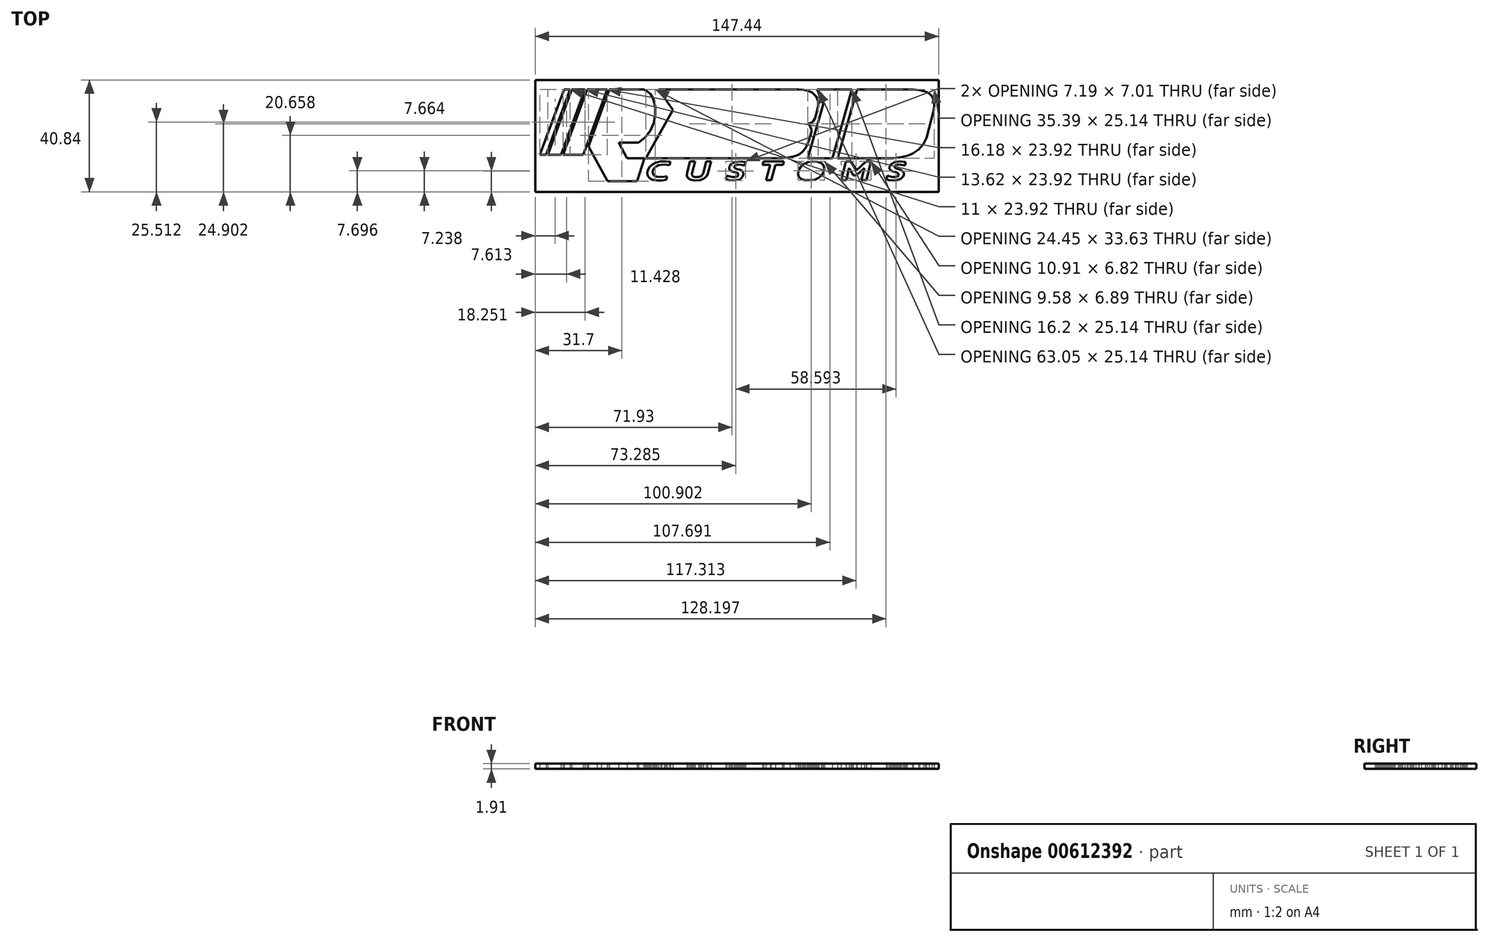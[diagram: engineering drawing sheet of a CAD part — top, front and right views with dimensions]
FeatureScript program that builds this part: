
annotation { "Feature Type Name" : "Feature", "Feature Type Description" : "" }
export const myFeature = defineFeature(function(context is Context, id is Id, definition is map)
    precondition{}
    {
        {
            var Q0;
            Q0=qCreatedBy(makeId("Top.planeOp"),FACE);
            var sketch = newSketch(context, id + "F0", { "sketchPlane" : qUnion([Q0])});
            skLineSegment(sketch, "E0", {"start": v(40.42, -9.55) * mm, "end": v(42.26, -9.55) * mm});
            skLineSegment(sketch, "E1", {"start": v(46.05, -16.37) * mm, "end": v(47.89, -16.37) * mm});
            skLineSegment(sketch, "E2", {"start": v(47.82, -9.55) * mm, "end": v(49.6, -9.55) * mm});
            skLineSegment(sketch, "E3", {"start": v(47.16, -11.96) * mm, "end": v(46.05, -16.37) * mm});
            skLineSegment(sketch, "E4", {"start": v(44.27, -14.59) * mm, "end": v(47.16, -11.96) * mm});
            skLineSegment(sketch, "E5", {"start": v(43.16, -14.59) * mm, "end": v(44.27, -14.59) * mm});
            skLineSegment(sketch, "E6", {"start": v(41.6, -11.98) * mm, "end": v(43.16, -14.59) * mm});
            skLineSegment(sketch, "E7", {"start": v(49.6, -9.55) * mm, "end": v(47.89, -16.37) * mm});
            skLineSegment(sketch, "E8", {"start": v(44.21, -12.83) * mm, "end": v(47.82, -9.55) * mm});
            skLineSegment(sketch, "E9", {"start": v(42.26, -9.55) * mm, "end": v(44.21, -12.83) * mm});
            skLineSegment(sketch, "E10", {"start": v(41.6, -11.98) * mm, "end": v(40.5, -16.37) * mm});
            skLineSegment(sketch, "E11", {"start": v(40.42, -9.55) * mm, "end": v(38.7, -16.37) * mm});
            skLineSegment(sketch, "E12", {"start": v(28.33, -9.55) * mm, "end": v(26.64, -9.76) * mm});
            skLineSegment(sketch, "E13", {"start": v(26.64, -9.76) * mm, "end": v(24.97, -10.5) * mm});
            skLineSegment(sketch, "E14", {"start": v(24.97, -10.5) * mm, "end": v(23.75, -11.65) * mm});
            skLineSegment(sketch, "E15", {"start": v(23.75, -11.65) * mm, "end": v(23.18, -12.71) * mm});
            skLineSegment(sketch, "E16", {"start": v(23.18, -12.71) * mm, "end": v(22.95, -13.91) * mm});
            skLineSegment(sketch, "E17", {"start": v(22.95, -13.91) * mm, "end": v(23.15, -15.07) * mm});
            skLineSegment(sketch, "E18", {"start": v(23.15, -15.07) * mm, "end": v(23.88, -15.86) * mm});
            skLineSegment(sketch, "E19", {"start": v(23.88, -15.86) * mm, "end": v(25.38, -16.36) * mm});
            skLineSegment(sketch, "E20", {"start": v(25.38, -16.36) * mm, "end": v(27.12, -16.44) * mm});
            skLineSegment(sketch, "E21", {"start": v(27.12, -16.44) * mm, "end": v(28.98, -16.25) * mm});
            skLineSegment(sketch, "E22", {"start": v(28.98, -16.25) * mm, "end": v(30.55, -15.5) * mm});
            skLineSegment(sketch, "E23", {"start": v(30.55, -15.5) * mm, "end": v(31.72, -14.43) * mm});
            skLineSegment(sketch, "E24", {"start": v(31.72, -14.43) * mm, "end": v(32.25, -13.43) * mm});
            skLineSegment(sketch, "E25", {"start": v(32.25, -13.43) * mm, "end": v(32.53, -12.09) * mm});
            skLineSegment(sketch, "E26", {"start": v(32.53, -12.09) * mm, "end": v(32.23, -10.87) * mm});
            skLineSegment(sketch, "E27", {"start": v(32.23, -10.87) * mm, "end": v(31.4, -10.13) * mm});
            skLineSegment(sketch, "E28", {"start": v(31.4, -10.13) * mm, "end": v(29.92, -9.63) * mm});
            skLineSegment(sketch, "E29", {"start": v(29.92, -9.63) * mm, "end": v(28.33, -9.55) * mm});
            skLineSegment(sketch, "E30", {"start": v(17.42, -10.84) * mm, "end": v(17.74, -9.55) * mm});
            skLineSegment(sketch, "E31", {"start": v(14.63, -10.84) * mm, "end": v(17.42, -10.84) * mm});
            skLineSegment(sketch, "E32", {"start": v(13.16, -16.37) * mm, "end": v(14.63, -10.84) * mm});
            skLineSegment(sketch, "E33", {"start": v(11.28, -16.37) * mm, "end": v(11.47, -16.37) * mm});
            skLineSegment(sketch, "E34", {"start": v(12.75, -10.84) * mm, "end": v(11.28, -16.37) * mm});
            skLineSegment(sketch, "E35", {"start": v(9.96, -10.84) * mm, "end": v(12.75, -10.84) * mm});
            skLineSegment(sketch, "E36", {"start": v(10.28, -9.55) * mm, "end": v(9.96, -10.84) * mm});
            skLineSegment(sketch, "E37", {"start": v(55.5, -14.69) * mm, "end": v(55.12, -16.02) * mm});
            skLineSegment(sketch, "E38", {"start": v(62.31, -9.82) * mm, "end": v(60.42, -9.53) * mm});
            skLineSegment(sketch, "E39", {"start": v(60.42, -9.53) * mm, "end": v(58.37, -9.72) * mm});
            skLineSegment(sketch, "E40", {"start": v(58.37, -9.72) * mm, "end": v(56.95, -10.49) * mm});
            skLineSegment(sketch, "E41", {"start": v(56.95, -10.49) * mm, "end": v(56.44, -11.2) * mm});
            skLineSegment(sketch, "E42", {"start": v(56.44, -11.2) * mm, "end": v(56.3, -12.06) * mm});
            skLineSegment(sketch, "E43", {"start": v(56.3, -12.06) * mm, "end": v(56.52, -12.6) * mm});
            skLineSegment(sketch, "E44", {"start": v(56.52, -12.6) * mm, "end": v(57.02, -12.95) * mm});
            skLineSegment(sketch, "E45", {"start": v(57.02, -12.95) * mm, "end": v(57.56, -13.17) * mm});
            skLineSegment(sketch, "E46", {"start": v(57.56, -13.17) * mm, "end": v(58.24, -13.4) * mm});
            skLineSegment(sketch, "E47", {"start": v(58.24, -13.4) * mm, "end": v(58.94, -13.62) * mm});
            skLineSegment(sketch, "E48", {"start": v(58.94, -13.62) * mm, "end": v(59.4, -13.82) * mm});
            skLineSegment(sketch, "E49", {"start": v(59.4, -13.82) * mm, "end": v(59.67, -14.18) * mm});
            skLineSegment(sketch, "E50", {"start": v(59.67, -14.18) * mm, "end": v(59.68, -14.56) * mm});
            skLineSegment(sketch, "E51", {"start": v(59.68, -14.56) * mm, "end": v(59.34, -14.98) * mm});
            skLineSegment(sketch, "E52", {"start": v(59.34, -14.98) * mm, "end": v(58.5, -15.25) * mm});
            skLineSegment(sketch, "E53", {"start": v(58.5, -15.25) * mm, "end": v(57.48, -15.22) * mm});
            skLineSegment(sketch, "E54", {"start": v(57.48, -15.22) * mm, "end": v(56.34, -15.01) * mm});
            skLineSegment(sketch, "E55", {"start": v(56.34, -15.01) * mm, "end": v(55.5, -14.69) * mm});
            skLineSegment(sketch, "E56", {"start": v(62.05, -11.04) * mm, "end": v(60.8, -10.76) * mm});
            skLineSegment(sketch, "E57", {"start": v(60.8, -10.76) * mm, "end": v(59.61, -10.67) * mm});
            skLineSegment(sketch, "E58", {"start": v(59.61, -10.67) * mm, "end": v(58.6, -10.88) * mm});
            skLineSegment(sketch, "E59", {"start": v(58.6, -10.88) * mm, "end": v(58.19, -11.37) * mm});
            skLineSegment(sketch, "E60", {"start": v(58.19, -11.37) * mm, "end": v(58.28, -11.84) * mm});
            skLineSegment(sketch, "E61", {"start": v(58.28, -11.84) * mm, "end": v(58.79, -12.13) * mm});
            skLineSegment(sketch, "E62", {"start": v(58.79, -12.13) * mm, "end": v(59.58, -12.38) * mm});
            skLineSegment(sketch, "E63", {"start": v(59.58, -12.38) * mm, "end": v(60.29, -12.61) * mm});
            skLineSegment(sketch, "E64", {"start": v(60.29, -12.61) * mm, "end": v(60.77, -12.83) * mm});
            skLineSegment(sketch, "E65", {"start": v(60.77, -12.83) * mm, "end": v(61.5, -13.41) * mm});
            skLineSegment(sketch, "E66", {"start": v(61.5, -13.41) * mm, "end": v(61.6, -14.2) * mm});
            skLineSegment(sketch, "E67", {"start": v(61.6, -14.2) * mm, "end": v(61.33, -15.03) * mm});
            skLineSegment(sketch, "E68", {"start": v(61.33, -15.03) * mm, "end": v(60.68, -15.74) * mm});
            skLineSegment(sketch, "E69", {"start": v(60.68, -15.74) * mm, "end": v(59.85, -16.19) * mm});
            skLineSegment(sketch, "E70", {"start": v(59.85, -16.19) * mm, "end": v(58.8, -16.44) * mm});
            skLineSegment(sketch, "E71", {"start": v(58.8, -16.44) * mm, "end": v(57.5, -16.54) * mm});
            skLineSegment(sketch, "E72", {"start": v(57.5, -16.54) * mm, "end": v(56.2, -16.35) * mm});
            skLineSegment(sketch, "E73", {"start": v(56.2, -16.35) * mm, "end": v(55.12, -16.02) * mm});
            skLineSegment(sketch, "E74", {"start": v(62.31, -9.82) * mm, "end": v(62.05, -11.04) * mm});
            skLineSegment(sketch, "E75", {"start": v(-3.1, -14.7) * mm, "end": v(-3.47, -16.03) * mm});
            skLineSegment(sketch, "E76", {"start": v(3.72, -9.83) * mm, "end": v(1.82, -9.54) * mm});
            skLineSegment(sketch, "E77", {"start": v(1.82, -9.54) * mm, "end": v(-0.22, -9.73) * mm});
            skLineSegment(sketch, "E78", {"start": v(-0.22, -9.73) * mm, "end": v(-1.65, -10.5) * mm});
            skLineSegment(sketch, "E79", {"start": v(-1.65, -10.5) * mm, "end": v(-2.15, -11.2) * mm});
            skLineSegment(sketch, "E80", {"start": v(-2.15, -11.2) * mm, "end": v(-2.3, -12.06) * mm});
            skLineSegment(sketch, "E81", {"start": v(-2.3, -12.06) * mm, "end": v(-2.07, -12.61) * mm});
            skLineSegment(sketch, "E82", {"start": v(-2.07, -12.61) * mm, "end": v(-1.57, -12.96) * mm});
            skLineSegment(sketch, "E83", {"start": v(-1.57, -12.96) * mm, "end": v(-1.04, -13.18) * mm});
            skLineSegment(sketch, "E84", {"start": v(-1.04, -13.18) * mm, "end": v(-0.35, -13.4) * mm});
            skLineSegment(sketch, "E85", {"start": v(-0.35, -13.4) * mm, "end": v(0.34, -13.63) * mm});
            skLineSegment(sketch, "E86", {"start": v(0.34, -13.63) * mm, "end": v(0.8, -13.83) * mm});
            skLineSegment(sketch, "E87", {"start": v(0.8, -13.83) * mm, "end": v(1.08, -14.19) * mm});
            skLineSegment(sketch, "E88", {"start": v(1.08, -14.19) * mm, "end": v(1.08, -14.57) * mm});
            skLineSegment(sketch, "E89", {"start": v(1.08, -14.57) * mm, "end": v(0.75, -15) * mm});
            skLineSegment(sketch, "E90", {"start": v(0.75, -15) * mm, "end": v(-0.1, -15.26) * mm});
            skLineSegment(sketch, "E91", {"start": v(-0.1, -15.26) * mm, "end": v(-1.11, -15.23) * mm});
            skLineSegment(sketch, "E92", {"start": v(-1.11, -15.23) * mm, "end": v(-2.25, -15.02) * mm});
            skLineSegment(sketch, "E93", {"start": v(-2.25, -15.02) * mm, "end": v(-3.1, -14.7) * mm});
            skLineSegment(sketch, "E94", {"start": v(3.46, -11.04) * mm, "end": v(2.2, -10.77) * mm});
            skLineSegment(sketch, "E95", {"start": v(2.2, -10.77) * mm, "end": v(1.02, -10.68) * mm});
            skLineSegment(sketch, "E96", {"start": v(1.02, -10.68) * mm, "end": v(0.02, -10.89) * mm});
            skLineSegment(sketch, "E97", {"start": v(0.02, -10.89) * mm, "end": v(-0.4, -11.38) * mm});
            skLineSegment(sketch, "E98", {"start": v(-0.4, -11.38) * mm, "end": v(-0.31, -11.85) * mm});
            skLineSegment(sketch, "E99", {"start": v(-0.31, -11.85) * mm, "end": v(0.2, -12.14) * mm});
            skLineSegment(sketch, "E100", {"start": v(0.2, -12.14) * mm, "end": v(0.99, -12.4) * mm});
            skLineSegment(sketch, "E101", {"start": v(0.99, -12.4) * mm, "end": v(1.7, -12.62) * mm});
            skLineSegment(sketch, "E102", {"start": v(1.7, -12.62) * mm, "end": v(2.18, -12.84) * mm});
            skLineSegment(sketch, "E103", {"start": v(2.18, -12.84) * mm, "end": v(2.9, -13.42) * mm});
            skLineSegment(sketch, "E104", {"start": v(2.9, -13.42) * mm, "end": v(3, -14.21) * mm});
            skLineSegment(sketch, "E105", {"start": v(3, -14.21) * mm, "end": v(2.73, -15.04) * mm});
            skLineSegment(sketch, "E106", {"start": v(2.73, -15.04) * mm, "end": v(2.08, -15.75) * mm});
            skLineSegment(sketch, "E107", {"start": v(2.08, -15.75) * mm, "end": v(1.25, -16.2) * mm});
            skLineSegment(sketch, "E108", {"start": v(1.25, -16.2) * mm, "end": v(0.2, -16.45) * mm});
            skLineSegment(sketch, "E109", {"start": v(0.2, -16.45) * mm, "end": v(-1.08, -16.55) * mm});
            skLineSegment(sketch, "E110", {"start": v(-1.08, -16.55) * mm, "end": v(-2.4, -16.36) * mm});
            skLineSegment(sketch, "E111", {"start": v(-2.4, -16.36) * mm, "end": v(-3.47, -16.03) * mm});
            skLineSegment(sketch, "E112", {"start": v(3.72, -9.83) * mm, "end": v(3.46, -11.04) * mm});
            skLineSegment(sketch, "E113", {"start": v(-10.66, -9.55) * mm, "end": v(-8.86, -9.55) * mm});
            skLineSegment(sketch, "E114", {"start": v(-15.84, -13.84) * mm, "end": v(-15.9, -14.3) * mm});
            skLineSegment(sketch, "E115", {"start": v(-15.9, -14.3) * mm, "end": v(-15.74, -14.76) * mm});
            skLineSegment(sketch, "E116", {"start": v(-15.74, -14.76) * mm, "end": v(-15.37, -15.07) * mm});
            skLineSegment(sketch, "E117", {"start": v(-15.37, -15.07) * mm, "end": v(-14.82, -15.24) * mm});
            skLineSegment(sketch, "E118", {"start": v(-14.82, -15.24) * mm, "end": v(-13.42, -15.23) * mm});
            skLineSegment(sketch, "E119", {"start": v(-13.42, -15.23) * mm, "end": v(-12.35, -14.87) * mm});
            skLineSegment(sketch, "E120", {"start": v(-12.35, -14.87) * mm, "end": v(-11.82, -14.03) * mm});
            skLineSegment(sketch, "E121", {"start": v(-17.67, -13.74) * mm, "end": v(-17.74, -14.84) * mm});
            skLineSegment(sketch, "E122", {"start": v(-17.74, -14.84) * mm, "end": v(-17.26, -15.76) * mm});
            skLineSegment(sketch, "E123", {"start": v(-17.26, -15.76) * mm, "end": v(-16.24, -16.3) * mm});
            skLineSegment(sketch, "E124", {"start": v(-16.24, -16.3) * mm, "end": v(-14.86, -16.5) * mm});
            skLineSegment(sketch, "E125", {"start": v(-14.86, -16.5) * mm, "end": v(-12.9, -16.4) * mm});
            skLineSegment(sketch, "E126", {"start": v(-12.9, -16.4) * mm, "end": v(-11.66, -15.9) * mm});
            skLineSegment(sketch, "E127", {"start": v(-11.66, -15.9) * mm, "end": v(-10.58, -15.08) * mm});
            skLineSegment(sketch, "E128", {"start": v(-10.58, -15.08) * mm, "end": v(-10.05, -14.17) * mm});
            skLineSegment(sketch, "E129", {"start": v(-8.86, -9.55) * mm, "end": v(-10.05, -14.17) * mm});
            skLineSegment(sketch, "E130", {"start": v(-10.66, -9.55) * mm, "end": v(-11.82, -14.03) * mm});
            skLineSegment(sketch, "E131", {"start": v(-14.73, -9.55) * mm, "end": v(-15.84, -13.84) * mm});
            skLineSegment(sketch, "E132", {"start": v(-16.58, -9.55) * mm, "end": v(-17.67, -13.74) * mm});
            skLineSegment(sketch, "E133", {"start": v(11.47, -16.37) * mm, "end": v(13.16, -16.37) * mm});
            skLineSegment(sketch, "E134", {"start": v(-16.58, -9.55) * mm, "end": v(-14.73, -9.55) * mm});
            skLineSegment(sketch, "E135", {"start": v(-24.91, -15.04) * mm, "end": v(-25.17, -16.21) * mm});
            skLineSegment(sketch, "E136", {"start": v(-23.75, -9.7) * mm, "end": v(-25.46, -9.49) * mm});
            skLineSegment(sketch, "E137", {"start": v(-25.46, -9.49) * mm, "end": v(-27.31, -9.52) * mm});
            skLineSegment(sketch, "E138", {"start": v(-27.31, -9.52) * mm, "end": v(-29.2, -10.02) * mm});
            skLineSegment(sketch, "E139", {"start": v(-29.2, -10.02) * mm, "end": v(-30.33, -10.61) * mm});
            skLineSegment(sketch, "E140", {"start": v(-30.33, -10.61) * mm, "end": v(-31.37, -11.6) * mm});
            skLineSegment(sketch, "E141", {"start": v(-31.37, -11.6) * mm, "end": v(-31.97, -12.67) * mm});
            skLineSegment(sketch, "E142", {"start": v(-31.97, -12.67) * mm, "end": v(-32.2, -13.7) * mm});
            skLineSegment(sketch, "E143", {"start": v(-32.2, -13.7) * mm, "end": v(-32.1, -14.5) * mm});
            skLineSegment(sketch, "E144", {"start": v(-32.1, -14.5) * mm, "end": v(-31.75, -15.24) * mm});
            skLineSegment(sketch, "E145", {"start": v(-31.75, -15.24) * mm, "end": v(-31.15, -15.81) * mm});
            skLineSegment(sketch, "E146", {"start": v(-31.15, -15.81) * mm, "end": v(-30.33, -16.2) * mm});
            skLineSegment(sketch, "E147", {"start": v(-30.33, -16.2) * mm, "end": v(-28.66, -16.51) * mm});
            skLineSegment(sketch, "E148", {"start": v(-28.66, -16.51) * mm, "end": v(-26.83, -16.51) * mm});
            skLineSegment(sketch, "E149", {"start": v(-26.83, -16.51) * mm, "end": v(-25.17, -16.21) * mm});
            skLineSegment(sketch, "E150", {"start": v(-24.03, -10.99) * mm, "end": v(-26.03, -10.68) * mm});
            skLineSegment(sketch, "E151", {"start": v(-26.03, -10.68) * mm, "end": v(-28.04, -10.96) * mm});
            skLineSegment(sketch, "E152", {"start": v(-28.04, -10.96) * mm, "end": v(-29.02, -11.46) * mm});
            skLineSegment(sketch, "E153", {"start": v(-29.02, -11.46) * mm, "end": v(-29.77, -12.2) * mm});
            skLineSegment(sketch, "E154", {"start": v(-29.77, -12.2) * mm, "end": v(-30.16, -12.97) * mm});
            skLineSegment(sketch, "E155", {"start": v(-30.16, -12.97) * mm, "end": v(-30.23, -13.75) * mm});
            skLineSegment(sketch, "E156", {"start": v(-30.23, -13.75) * mm, "end": v(-29.78, -14.65) * mm});
            skLineSegment(sketch, "E157", {"start": v(-29.78, -14.65) * mm, "end": v(-28.8, -15.1) * mm});
            skLineSegment(sketch, "E158", {"start": v(-28.8, -15.1) * mm, "end": v(-26.94, -15.3) * mm});
            skLineSegment(sketch, "E159", {"start": v(-26.94, -15.3) * mm, "end": v(-24.91, -15.04) * mm});
            skLineSegment(sketch, "E160", {"start": v(-23.75, -9.7) * mm, "end": v(-24.03, -10.99) * mm});
            skLineSegment(sketch, "E161", {"start": v(69.84, -0.9) * mm, "end": v(68.76, -3.12) * mm});
            skLineSegment(sketch, "E162", {"start": v(68.76, -3.12) * mm, "end": v(67, -5.17) * mm});
            skLineSegment(sketch, "E163", {"start": v(67, -5.17) * mm, "end": v(64.73, -6.7) * mm});
            skLineSegment(sketch, "E164", {"start": v(64.73, -6.7) * mm, "end": v(62.78, -7.48) * mm});
            skLineSegment(sketch, "E165", {"start": v(62.78, -7.48) * mm, "end": v(60.46, -8.02) * mm});
            skLineSegment(sketch, "E166", {"start": v(60.46, -8.02) * mm, "end": v(57.74, -8.33) * mm});
            skLineSegment(sketch, "E167", {"start": v(42.63, 16.81) * mm, "end": v(29.83, 16.81) * mm});
            skLineSegment(sketch, "E168", {"start": v(37.34, -8.33) * mm, "end": v(57.74, -8.33) * mm});
            skLineSegment(sketch, "E169", {"start": v(26.43, -8.33) * mm, "end": v(35.44, -8.33) * mm});
            skLineSegment(sketch, "E170", {"start": v(23.18, 16.81) * mm, "end": v(-0.77, 16.81) * mm});
            skLineSegment(sketch, "E171", {"start": v(-8.5, 16.81) * mm, "end": v(-28.07, 16.81) * mm});
            skLineSegment(sketch, "E172", {"start": v(2.73, -8.33) * mm, "end": v(17.25, -8.33) * mm});
            skLineSegment(sketch, "E173", {"start": v(-22.78, 9.31) * mm, "end": v(-32.76, -8.33) * mm});
            skLineSegment(sketch, "E174", {"start": v(29.83, 16.81) * mm, "end": v(32.18, 11.5) * mm});
            skLineSegment(sketch, "E175", {"start": v(32.18, 11.5) * mm, "end": v(26.43, -8.33) * mm});
            skLineSegment(sketch, "E176", {"start": v(42.63, 16.81) * mm, "end": v(35.44, -8.33) * mm});
            skLineSegment(sketch, "E177", {"start": v(44.53, 16.81) * mm, "end": v(37.34, -8.33) * mm});
            skLineSegment(sketch, "E178", {"start": v(72.6, 9.4) * mm, "end": v(72.73, 11.14) * mm});
            skLineSegment(sketch, "E179", {"start": v(72.73, 11.14) * mm, "end": v(72.5, 12.82) * mm});
            skLineSegment(sketch, "E180", {"start": v(72.5, 12.82) * mm, "end": v(71.77, 14.33) * mm});
            skLineSegment(sketch, "E181", {"start": v(71.77, 14.33) * mm, "end": v(70.74, 15.37) * mm});
            skLineSegment(sketch, "E182", {"start": v(70.74, 15.37) * mm, "end": v(69.33, 16.02) * mm});
            skLineSegment(sketch, "E183", {"start": v(69.33, 16.02) * mm, "end": v(67.4, 16.56) * mm});
            skLineSegment(sketch, "E184", {"start": v(67.4, 16.56) * mm, "end": v(65.13, 16.81) * mm});
            skLineSegment(sketch, "E185", {"start": v(72.6, 9.4) * mm, "end": v(69.84, -0.9) * mm});
            skLineSegment(sketch, "E186", {"start": v(26.33, 4.26) * mm, "end": v(27.18, 4.4) * mm});
            skLineSegment(sketch, "E187", {"start": v(27.18, 4.4) * mm, "end": v(27.93, 4.66) * mm});
            skLineSegment(sketch, "E188", {"start": v(27.93, 4.66) * mm, "end": v(28.5, 5.19) * mm});
            skLineSegment(sketch, "E189", {"start": v(28.5, 5.19) * mm, "end": v(29.07, 6.28) * mm});
            skLineSegment(sketch, "E190", {"start": v(29.07, 6.28) * mm, "end": v(29.82, 8.46) * mm});
            skLineSegment(sketch, "E191", {"start": v(29.82, 8.46) * mm, "end": v(30.3, 10.75) * mm});
            skLineSegment(sketch, "E192", {"start": v(30.3, 10.75) * mm, "end": v(30.27, 12.45) * mm});
            skLineSegment(sketch, "E193", {"start": v(30.27, 12.45) * mm, "end": v(29.52, 14.24) * mm});
            skLineSegment(sketch, "E194", {"start": v(29.52, 14.24) * mm, "end": v(28.06, 15.6) * mm});
            skLineSegment(sketch, "E195", {"start": v(28.06, 15.6) * mm, "end": v(26.62, 16.23) * mm});
            skLineSegment(sketch, "E196", {"start": v(26.62, 16.23) * mm, "end": v(24.88, 16.66) * mm});
            skLineSegment(sketch, "E197", {"start": v(24.88, 16.66) * mm, "end": v(23.18, 16.81) * mm});
            skLineSegment(sketch, "E198", {"start": v(26.33, 4.26) * mm, "end": v(26.98, 3.8) * mm});
            skLineSegment(sketch, "E199", {"start": v(26.98, 3.8) * mm, "end": v(27.5, 3.08) * mm});
            skLineSegment(sketch, "E200", {"start": v(27.5, 3.08) * mm, "end": v(27.8, 2.23) * mm});
            skLineSegment(sketch, "E201", {"start": v(27.8, 2.23) * mm, "end": v(27.8, 1.48) * mm});
            skLineSegment(sketch, "E202", {"start": v(27.8, 1.48) * mm, "end": v(27.47, 0.1) * mm});
            skLineSegment(sketch, "E203", {"start": v(27.47, 0.1) * mm, "end": v(26.82, -1.9) * mm});
            skLineSegment(sketch, "E204", {"start": v(26.82, -1.9) * mm, "end": v(26.2, -3.5) * mm});
            skLineSegment(sketch, "E205", {"start": v(26.2, -3.5) * mm, "end": v(25.56, -4.77) * mm});
            skLineSegment(sketch, "E206", {"start": v(25.56, -4.77) * mm, "end": v(24.6, -5.92) * mm});
            skLineSegment(sketch, "E207", {"start": v(24.6, -5.92) * mm, "end": v(23.49, -6.81) * mm});
            skLineSegment(sketch, "E208", {"start": v(23.49, -6.81) * mm, "end": v(22.2, -7.5) * mm});
            skLineSegment(sketch, "E209", {"start": v(22.2, -7.5) * mm, "end": v(19.95, -8) * mm});
            skLineSegment(sketch, "E210", {"start": v(19.95, -8) * mm, "end": v(17.25, -8.33) * mm});
            skLineSegment(sketch, "E211", {"start": v(-33.51, 16.81) * mm, "end": v(-32.12, 16.04) * mm});
            skLineSegment(sketch, "E212", {"start": v(-32.12, 16.04) * mm, "end": v(-30.97, 14.97) * mm});
            skLineSegment(sketch, "E213", {"start": v(-30.97, 14.97) * mm, "end": v(-30.1, 13.47) * mm});
            skLineSegment(sketch, "E214", {"start": v(-30.1, 13.47) * mm, "end": v(-29.23, 10.61) * mm});
            skLineSegment(sketch, "E215", {"start": v(-29.23, 10.61) * mm, "end": v(-29.24, 7.62) * mm});
            skLineSegment(sketch, "E216", {"start": v(-29.24, 7.62) * mm, "end": v(-29.86, 4.52) * mm});
            skLineSegment(sketch, "E217", {"start": v(-29.86, 4.52) * mm, "end": v(-31.1, 1.59) * mm});
            skLineSegment(sketch, "E218", {"start": v(-31.1, 1.59) * mm, "end": v(-33.02, -0.8) * mm});
            skLineSegment(sketch, "E219", {"start": v(-33.02, -0.8) * mm, "end": v(-35.37, -2.66) * mm});
            skLineSegment(sketch, "E220", {"start": v(-33.51, 16.81) * mm, "end": v(-46.1, 16.81) * mm});
            skLineSegment(sketch, "E221", {"start": v(-5.07, -8.33) * mm, "end": v(2.3, -8.33) * mm});
            skLineSegment(sketch, "E222", {"start": v(38.7, -16.37) * mm, "end": v(40.5, -16.37) * mm});
            skLineSegment(sketch, "E223", {"start": v(28.33, -9.55) * mm, "end": v(29.1, -9.55) * mm});
            skLineSegment(sketch, "E224", {"start": v(10.28, -9.55) * mm, "end": v(17.74, -9.55) * mm});
            skLineSegment(sketch, "E225", {"start": v(1.03, -9.55) * mm, "end": v(2.06, -9.55) * mm});
            skLineSegment(sketch, "E226", {"start": v(65.13, 16.81) * mm, "end": v(44.53, 16.81) * mm});
            skLineSegment(sketch, "E227", {"start": v(-49, 8.95) * mm, "end": v(-46.1, 16.81) * mm});
            skLineSegment(sketch, "E228", {"start": v(-50.53, 4.54) * mm, "end": v(-53.69, -4.04) * mm});
            skLineSegment(sketch, "E229", {"start": v(-53.69, -4.04) * mm, "end": v(-46.73, -16.81) * mm});
            skLineSegment(sketch, "E230", {"start": v(-46.73, -16.81) * mm, "end": v(-35.85, -16.81) * mm});
            skLineSegment(sketch, "E231", {"start": v(-35.85, -16.81) * mm, "end": v(-33.28, -8.33) * mm});
            skLineSegment(sketch, "E232", {"start": v(-33.28, -8.33) * mm, "end": v(-39.56, -8.33) * mm});
            skLineSegment(sketch, "E233", {"start": v(-39.56, -8.33) * mm, "end": v(-42.64, -2.66) * mm});
            skLineSegment(sketch, "E234", {"start": v(-42.64, -2.66) * mm, "end": v(-35.37, -2.66) * mm});
            skLineSegment(sketch, "E235", {"start": v(-32.76, -8.33) * mm, "end": v(-22.07, -8.33) * mm});
            skLineSegment(sketch, "E236", {"start": v(-28.07, 16.81) * mm, "end": v(-22.78, 9.31) * mm});
            skLineSegment(sketch, "E237", {"start": v(-22.07, -8.33) * mm, "end": v(-5.07, -8.33) * mm});
            skLineSegment(sketch, "E238", {"start": v(-49, 8.95) * mm, "end": v(-50.53, 4.54) * mm});
            skLineSegment(sketch, "E239", {"start": v(-8.5, 16.81) * mm, "end": v(-0.77, 16.81) * mm});
            skLineSegment(sketch, "E240", {"start": v(2.3, -8.33) * mm, "end": v(2.73, -8.33) * mm});
            skLineSegment(sketch, "E241", {"start": v(-71.42, -7.1) * mm, "end": v(-62.62, 16.81) * mm});
            skLineSegment(sketch, "E242", {"start": v(-55.62, -7.1) * mm, "end": v(-63, -7.1) * mm});
            skLineSegment(sketch, "E243", {"start": v(-60.42, 16.81) * mm, "end": v(-69.22, -7.1) * mm});
            skLineSegment(sketch, "E244", {"start": v(-68.54, -7.1) * mm, "end": v(-59.74, 16.81) * mm});
            skLineSegment(sketch, "E245", {"start": v(-54.92, 16.81) * mm, "end": v(-63.73, -7.1) * mm});
            skLineSegment(sketch, "E246", {"start": v(-63, -7.1) * mm, "end": v(-54.2, 16.81) * mm});
            skLineSegment(sketch, "E247", {"start": v(-46.82, 16.81) * mm, "end": v(-55.62, -7.1) * mm});
            skLineSegment(sketch, "E248.trimOffspring", {"start": v(-60.42, 16.81) * mm, "end": v(-62.62, 16.81) * mm});
            skLineSegment(sketch, "E249.trimOffspring", {"start": v(-54.92, 16.81) * mm, "end": v(-59.74, 16.81) * mm});
            skLineSegment(sketch, "E250.trimOffspring", {"start": v(-46.82, 16.81) * mm, "end": v(-54.2, 16.81) * mm});
            skLineSegment(sketch, "E251.trimOffspring", {"start": v(-63.73, -7.1) * mm, "end": v(-68.54, -7.1) * mm});
            skLineSegment(sketch, "E252.trimOffspring", {"start": v(-69.22, -7.1) * mm, "end": v(-71.42, -7.1) * mm});
            skSolve(sketch);
        }
        {
            var Q0;
            Q0=qCreatedBy(makeId("Top.planeOp"),FACE);
            var sketch = newSketch(context, id + "F1", { "sketchPlane" : qUnion([Q0])});
            skLineSegment(sketch, "E253.bottom", {"start": v(-73.16, 20.18) * mm, "end": v(74.28, 20.18) * mm});
            skLineSegment(sketch, "E253.top", {"start": v(-73.16, -20.66) * mm, "end": v(74.28, -20.66) * mm});
            skLineSegment(sketch, "E253.left", {"start": v(-73.16, 20.18) * mm, "end": v(-73.16, -20.66) * mm});
            skLineSegment(sketch, "E253.right", {"start": v(74.28, 20.18) * mm, "end": v(74.28, -20.66) * mm});
            skSolve(sketch);
        }
        {
            var Q0;
            Q0 = qSketchRegion(id + "F0", true);
            var Q1;
            Q1 = qSketchRegion(id + "F1", true);
            extrude(context, id + "F2", {"entities" : qUnion([Q0, Q1]), "depth" : 1.9 * mm, "offsetDistance" : 25.4 * mm});
        }
        {
            var Q0;
            Q0 = qSketchRegion(id + "F0", true);
            extrude(context, id + "F3", {"entities" : qUnion([Q0]), "operationType" : NewBodyOperationType.REMOVE, "endBound" : BoundingType.THROUGH_ALL, "depth" : 25.4 * mm, "offsetDistance" : 25.4 * mm});
        }
    });
